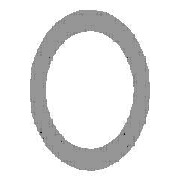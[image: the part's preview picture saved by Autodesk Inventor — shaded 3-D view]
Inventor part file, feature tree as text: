
AUTODESK INVENTOR PART (.ipt)
format: ipt  version: 2013 (Build 170138000, 138)  size: 122,368 bytes
history: native  units: mm (DEFAULTED — no unit token found)
features: other x4, plane x4, sketch x4, extrude x1
ambient origin geometry x8: Origin, YZ Plane, XZ Plane, XY Plane, X Axis, Y Axis, Z Axis, Center Point
bodies: Solid1 (feature_tree), Body (feature_tree)
feature tree (13):
  parser-record x1  (decoder bookkeeping rows leaked as tree rows — omitted from the tree; the rows remain in map.json)
  other  "Driven Length"
  other  "Start plane"
  other  "End plane"
  plane  "Work Plane4"
  plane  "Work Plane5"
  plane  "Work Plane6"
  extrude  "Extrusion2"  Depth=3.556mm
  sketch  "Sketch"  dims[d5=234.95mm d6=90.0deg d7=234.95mm d8=3.302mm d9=0.0mm]
  sketch  "Sketch3"  dims[d0=42.164mm d1=3.556mm]
  plane  "Work Plane3"
  sketch  "Sketch4"  dims[d2=234.95mm d3=0.0mm]
  sketch  "Sketch5"  dims[d4=-0.0mm]
